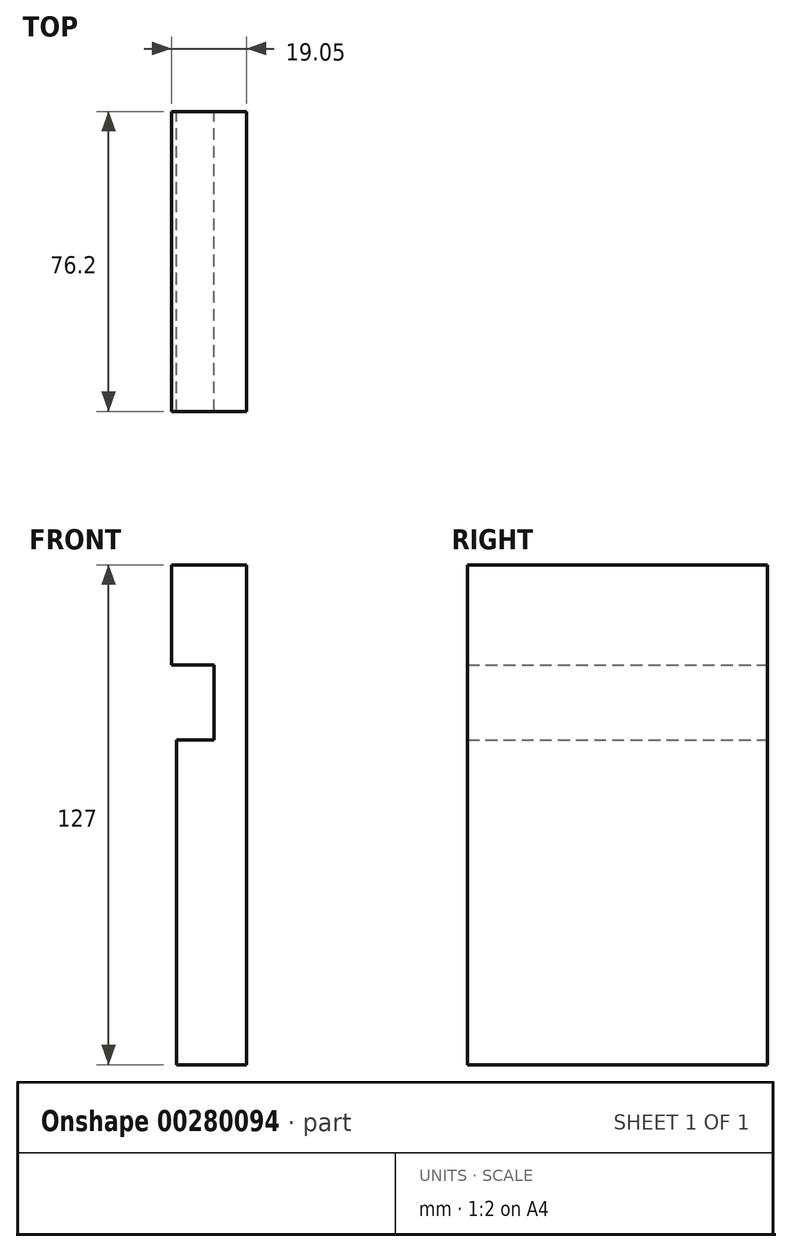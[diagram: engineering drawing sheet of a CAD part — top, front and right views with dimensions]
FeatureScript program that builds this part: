
annotation { "Feature Type Name" : "Feature", "Feature Type Description" : "" }
export const myFeature = defineFeature(function(context is Context, id is Id, definition is map)
    precondition{}
    {
        {
            var Q0;
            Q0=qCreatedBy(makeId("Front.planeOp"),FACE);
            var sketch = newSketch(context, id + "F0", { "sketchPlane" : qUnion([Q0])});
            skLineSegment(sketch, "E0", {"start": v(0, 0) * mm, "end": v(0, 127) * mm});
            skLineSegment(sketch, "E1", {"start": v(0, 127) * mm, "end": v(-19.05, 127) * mm});
            skLineSegment(sketch, "E2", {"start": v(-19.05, 127) * mm, "end": v(-19.05, 101.6) * mm});
            skLineSegment(sketch, "E3", {"start": v(-19.05, 101.6) * mm, "end": v(-8.23, 101.6) * mm});
            skLineSegment(sketch, "E4", {"start": v(-8.23, 101.6) * mm, "end": v(-8.23, 82.55) * mm});
            skLineSegment(sketch, "E5", {"start": v(-8.23, 82.55) * mm, "end": v(-17.76, 82.55) * mm});
            skLineSegment(sketch, "E6", {"start": v(-17.76, 82.55) * mm, "end": v(-17.76, 0) * mm});
            skLineSegment(sketch, "E7", {"start": v(-17.76, 0) * mm, "end": v(0, 0) * mm});
            skSolve(sketch);
        }
        {
            var Q0;
            Q0 = qSketchRegion(id + "F0", true);
            extrude(context, id + "F1", {"entities" : qUnion([Q0]), "depth" : 76.2 * mm});
        }
    });
